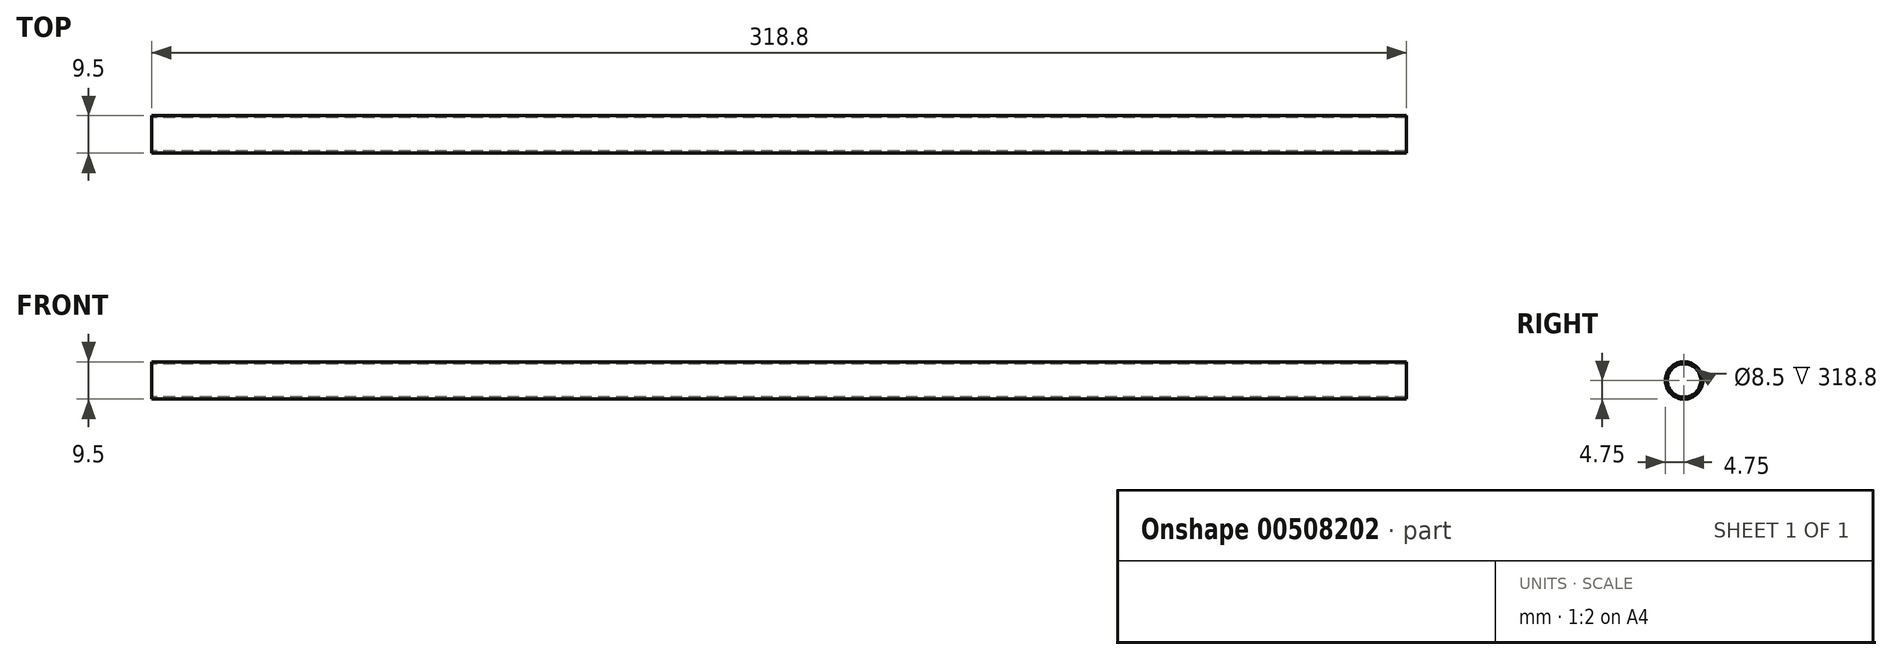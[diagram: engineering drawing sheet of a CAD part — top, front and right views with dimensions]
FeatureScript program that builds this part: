
annotation { "Feature Type Name" : "Feature", "Feature Type Description" : "" }
export const myFeature = defineFeature(function(context is Context, id is Id, definition is map)
    precondition{}
    {
        {
            var Q0;
            Q0=qCreatedBy(makeId("Right.planeOp"),FACE);
            var sketch = newSketch(context, id + "F0", { "sketchPlane" : qUnion([Q0])});
            skCircle(sketch, "E0", {"center": v(0, 0) * mm, "radius": 4.75 * mm});
            skCircle(sketch, "E1", {"center": v(0, 0) * mm, "radius": 4.25 * mm});
            skSolve(sketch);
        }
        {
            var Q0;
            Q0 = qSketchRegion(id + "F0", true);
            extrude(context, id + "F1", {"entities" : qUnion([Q0]), "depth" : 318.8 * mm, "offsetDistance" : 25 * mm});
        }
    });
